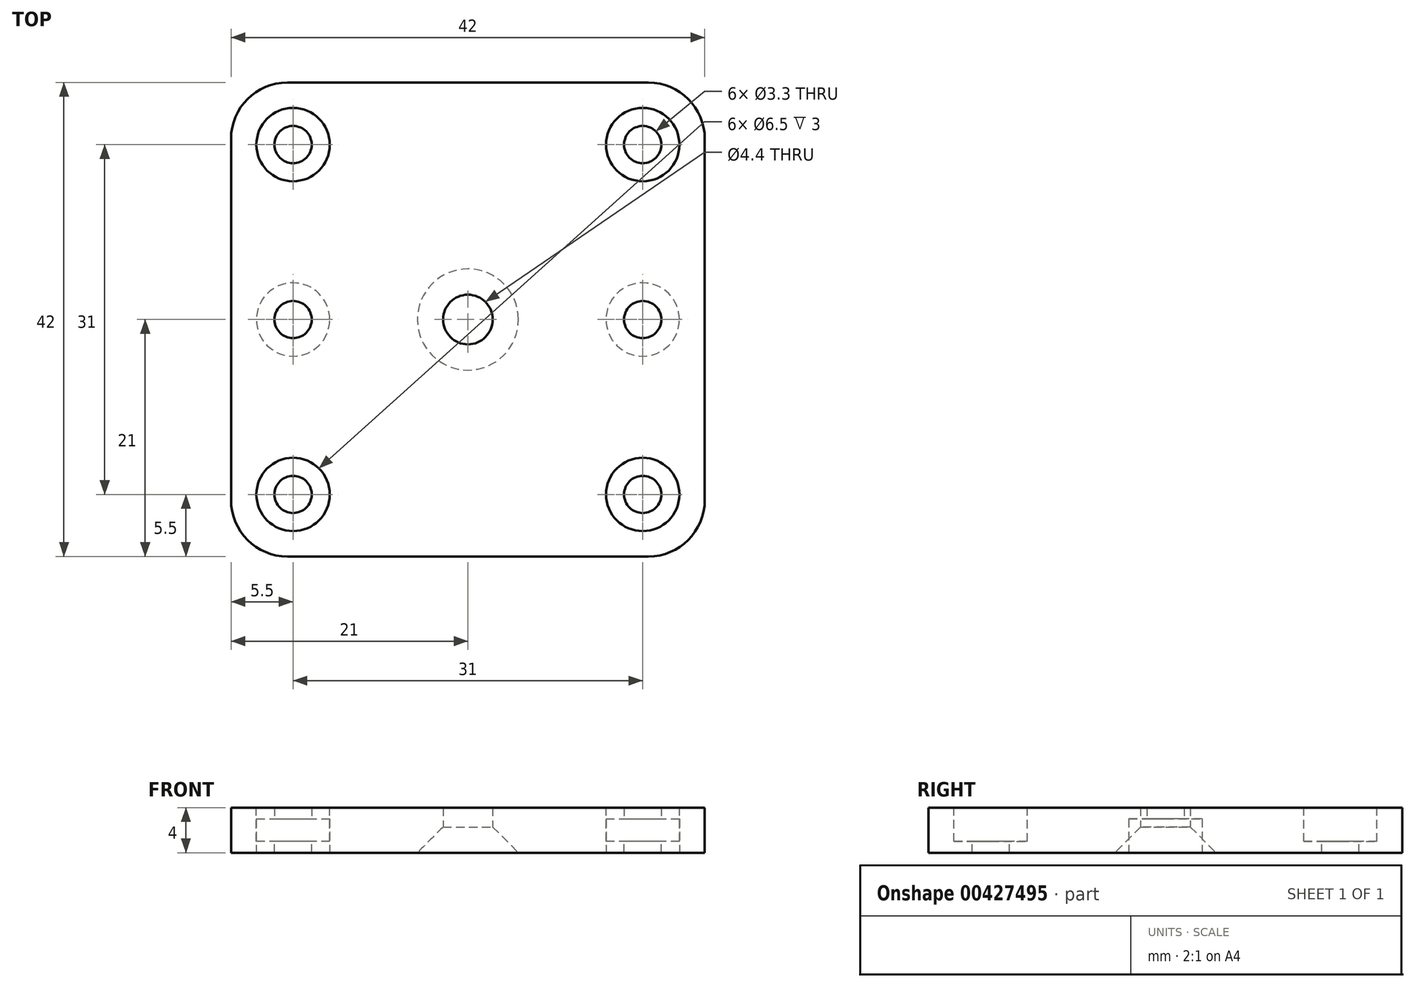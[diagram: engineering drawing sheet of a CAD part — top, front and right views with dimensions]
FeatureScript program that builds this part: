
annotation { "Feature Type Name" : "Feature", "Feature Type Description" : "" }
export const myFeature = defineFeature(function(context is Context, id is Id, definition is map)
    precondition{}
    {
        {
            var Q0;
            Q0=qCreatedBy(makeId("Top.planeOp"),FACE);
            var sketch = newSketch(context, id + "F0", { "sketchPlane" : qUnion([Q0])});
            skLineSegment(sketch, "E0.bottom", {"start": v(21, 21) * mm, "end": v(-21, 21) * mm});
            skLineSegment(sketch, "E0.top", {"start": v(21, -21) * mm, "end": v(-21, -21) * mm});
            skLineSegment(sketch, "E0.left", {"start": v(21, 21) * mm, "end": v(21, -21) * mm});
            skLineSegment(sketch, "E0.right", {"start": v(-21, 21) * mm, "end": v(-21, -21) * mm});
            skPoint(sketch, "E0.middle", {"position": v(0, 0) * mm});
            skSolve(sketch);
        }
        {
            var Q0;
            Q0=makeQuery(id+"F0.imprint","IMPRINT",FACE,{"disambiguationData":[TD([[makeQuery(id+"F0.imprint","IMPRINT",EDGE,{"derivedFrom":sQuery(id+"F0.wireOp",EDGE,"E0.bottom")}),1.0]])]});
            extrude(context, id + "F1", {"entities" : qUnion([Q0]), "depth" : 4 * mm});
        }
        {
            var Q0;
            Q0=makeQuery(id+"F1.opExtrude","CAP_FACE",FACE,{"disambiguationData":[OSD([sQuery(id+"F0.wireOp",EDGE,"E0.bottom"),sQuery(id+"F0.wireOp",EDGE,"E0.top"),sQuery(id+"F0.wireOp",EDGE,"E0.left"),sQuery(id+"F0.wireOp",EDGE,"E0.right")])],"isStart":false});
            var sketch = newSketch(context, id + "F2", { "sketchPlane" : qUnion([Q0])});
            skLineSegment(sketch, "E1.bottom", {"start": v(15.5, 15.5) * mm, "end": v(-15.5, 15.5) * mm});
            skLineSegment(sketch, "E1.top", {"start": v(15.5, -15.5) * mm, "end": v(-15.5, -15.5) * mm});
            skLineSegment(sketch, "E1.left", {"start": v(15.5, 15.5) * mm, "end": v(15.5, -15.5) * mm});
            skLineSegment(sketch, "E1.right", {"start": v(-15.5, 15.5) * mm, "end": v(-15.5, -15.5) * mm});
            skSolve(sketch);
        }
        {
            var Q0;
            Q0=makeQuery(id+"F1.opExtrude","SWEPT_EDGE",EDGE,{"disambiguationData":[OSD([sQuery(id+"F0.wireOp",EDGE,"E0.bottom"),sQuery(id+"F0.wireOp",EDGE,"E0.right")])]});
            var Q1;
            Q1=makeQuery(id+"F1.opExtrude","SWEPT_EDGE",EDGE,{"disambiguationData":[OSD([sQuery(id+"F0.wireOp",EDGE,"E0.top"),sQuery(id+"F0.wireOp",EDGE,"E0.right")])]});
            var Q2;
            Q2=makeQuery(id+"F1.opExtrude","SWEPT_EDGE",EDGE,{"disambiguationData":[OSD([sQuery(id+"F0.wireOp",EDGE,"E0.top"),sQuery(id+"F0.wireOp",EDGE,"E0.left")])]});
            var Q3;
            Q3=makeQuery(id+"F1.opExtrude","SWEPT_EDGE",EDGE,{"disambiguationData":[OSD([sQuery(id+"F0.wireOp",EDGE,"E0.bottom"),sQuery(id+"F0.wireOp",EDGE,"E0.left")])]});
            fillet(context, id + "F3", {"entities" : qUnion([Q0, Q1, Q2, Q3]), "radius" : 5 * mm, "tangentPropagation" : true, "allowEdgeOverflow" : false});
        }
        {
            var Q0;
            Q0=sQuery(id+"F2.wireOp",VERTEX,"E1.right.start");
            var Q1;
            Q1=sQuery(id+"F2.wireOp",VERTEX,"E1.left.start");
            var Q2;
            Q2=sQuery(id+"F2.wireOp",VERTEX,"E1.left.end");
            var Q3;
            Q3=sQuery(id+"F2.wireOp",VERTEX,"E1.top.end");
            var Q4;
            Q4=makeQuery(id+"F1.opExtrude","SWEPT_BODY",BODY,{"disambiguationData":[OSD([sQuery(id+"F0.wireOp",EDGE,"E0.bottom"),sQuery(id+"F0.wireOp",EDGE,"E0.top"),sQuery(id+"F0.wireOp",EDGE,"E0.left"),sQuery(id+"F0.wireOp",EDGE,"E0.right")])]});
            hole(context, id + "F4", {"style" : HoleStyle.C_BORE, "endStyle" : HoleEndStyle.THROUGH, "standardTappedOrClearance" : lookupTablePath({ "standard" : "ISO", "fit" : "Normal", "size" : "M3", "type" : "Clearance" }), "standardBlindInLast" : lookupTablePath({ "fit" : "Standard", "standard" : "ISO", "size" : "M3", "type" : "Clearance" }), "holeDiameter" : 3.3 * mm, "cBoreDiameter" : 6.5 * mm, "cBoreDepth" : 3 * mm, "isTappedThrough" : true, "tappedDepth" : 12 * mm, "tapClearance" : 3, "locations" : qUnion([Q0, Q1, Q2, Q3]), "scope" : qUnion([Q4])});
        }
        {
            var Q0;
            Q0=makeQuery(id+"F1.opExtrude","CAP_FACE",FACE,{"disambiguationData":[OSD([sQuery(id+"F0.wireOp",EDGE,"E0.bottom"),sQuery(id+"F0.wireOp",EDGE,"E0.top"),sQuery(id+"F0.wireOp",EDGE,"E0.left"),sQuery(id+"F0.wireOp",EDGE,"E0.right")])],"isStart":true});
            var sketch = newSketch(context, id + "F5", { "sketchPlane" : qUnion([Q0])});
            skCircle(sketch, "E2", {"center": v(0, 0) * mm, "radius": 8.54 * mm});
            skSolve(sketch);
        }
        {
            var Q0;
            Q0=sQuery(id+"F5.wireOp",VERTEX,"E2.center");
            var Q1;
            Q1=makeQuery(id+"F1.opExtrude","SWEPT_BODY",BODY,{"disambiguationData":[OSD([sQuery(id+"F0.wireOp",EDGE,"E0.bottom"),sQuery(id+"F0.wireOp",EDGE,"E0.top"),sQuery(id+"F0.wireOp",EDGE,"E0.left"),sQuery(id+"F0.wireOp",EDGE,"E0.right")])]});
            hole(context, id + "F6", {"style" : HoleStyle.C_SINK, "endStyle" : HoleEndStyle.THROUGH, "standardTappedOrClearance" : lookupTablePath({ "standard" : "ISO", "fit" : "Normal", "size" : "M4", "type" : "Clearance" }), "standardBlindInLast" : lookupTablePath({ "fit" : "Standard", "standard" : "ISO", "size" : "M4", "type" : "Clearance" }), "holeDiameter" : 4.4 * mm, "cSinkDiameter" : 8.96 * mm, "cSinkAngle" : 90 * degree, "isTappedThrough" : true, "tappedDepth" : 12 * mm, "tapClearance" : 3, "locations" : qUnion([Q0]), "scope" : qUnion([Q1])});
        }
        {
            var Q0;
            Q0=makeQuery(id+"F1.opExtrude","CAP_FACE",FACE,{"disambiguationData":[OSD([sQuery(id+"F0.wireOp",EDGE,"E0.bottom"),sQuery(id+"F0.wireOp",EDGE,"E0.top"),sQuery(id+"F0.wireOp",EDGE,"E0.left"),sQuery(id+"F0.wireOp",EDGE,"E0.right")])],"isStart":true});
            var sketch = newSketch(context, id + "F7", { "sketchPlane" : qUnion([Q0])});
            skLineSegment(sketch, "E3", {"start": v(-15.5, 0) * mm, "end": v(15.5, 0) * mm});
            skSolve(sketch);
        }
        {
            var Q0;
            Q0=sQuery(id+"F7.wireOp",VERTEX,"E3.start");
            var Q1;
            Q1=sQuery(id+"F7.wireOp",VERTEX,"E3.end");
            var Q2;
            Q2=makeQuery(id+"F1.opExtrude","SWEPT_BODY",BODY,{"disambiguationData":[OSD([sQuery(id+"F0.wireOp",EDGE,"E0.bottom"),sQuery(id+"F0.wireOp",EDGE,"E0.top"),sQuery(id+"F0.wireOp",EDGE,"E0.left"),sQuery(id+"F0.wireOp",EDGE,"E0.right")])]});
            hole(context, id + "F8", {"style" : HoleStyle.C_BORE, "endStyle" : HoleEndStyle.THROUGH, "standardTappedOrClearance" : lookupTablePath({ "standard" : "ISO", "fit" : "Normal", "size" : "M3", "type" : "Clearance" }), "standardBlindInLast" : lookupTablePath({ "fit" : "Standard", "standard" : "ISO", "size" : "M3", "type" : "Clearance" }), "holeDiameter" : 3.3 * mm, "cBoreDiameter" : 6.5 * mm, "cBoreDepth" : 3 * mm, "isTappedThrough" : true, "tappedDepth" : 12 * mm, "tapClearance" : 3, "locations" : qUnion([Q0, Q1]), "scope" : qUnion([Q2])});
        }
    });
